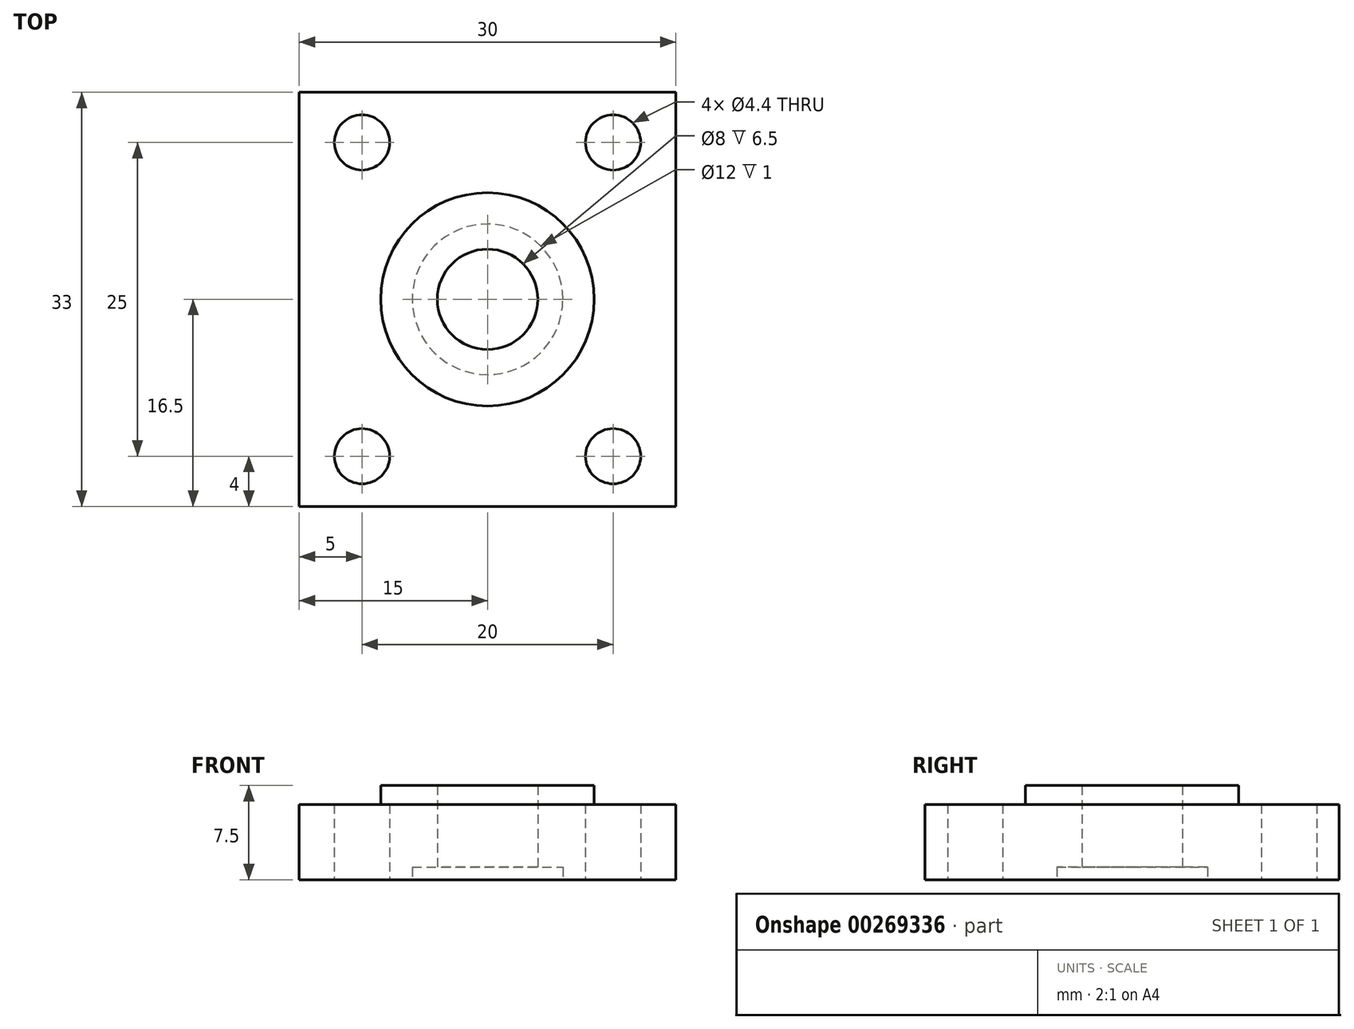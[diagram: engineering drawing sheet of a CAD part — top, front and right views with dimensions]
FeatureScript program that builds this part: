
annotation { "Feature Type Name" : "Feature", "Feature Type Description" : "" }
export const myFeature = defineFeature(function(context is Context, id is Id, definition is map)
    precondition{}
    {
        {
            var Q0;
            Q0=qCreatedBy(makeId("Top.planeOp"),FACE);
            var sketch = newSketch(context, id + "F0", { "sketchPlane" : qUnion([Q0])});
            skLineSegment(sketch, "E0.bottom", {"start": v(-15, -16.5) * mm, "end": v(15, -16.5) * mm});
            skLineSegment(sketch, "E0.top", {"start": v(-15, 16.5) * mm, "end": v(15, 16.5) * mm});
            skLineSegment(sketch, "E0.left", {"start": v(-15, -16.5) * mm, "end": v(-15, 16.5) * mm});
            skLineSegment(sketch, "E0.right", {"start": v(15, -16.5) * mm, "end": v(15, 16.5) * mm});
            skPoint(sketch, "E0.middle", {"position": v(0, 0) * mm});
            skCircle(sketch, "E1", {"center": v(0, 0) * mm, "radius": 4 * mm});
            skSolve(sketch);
        }
        {
            var Q0;
            Q0=qSketchRegion(id+"F0",true);
            extrude(context, id + "F1", {"entities" : qUnion([Q0]), "depth" : 6 * mm});
        }
        {
            var Q0;
            Q0=makeQuery(id+"F1.opExtrude","CAP_FACE",FACE,{"disambiguationData":[OSD([sQuery(id+"F0.wireOp",EDGE,"E0.bottom"),sQuery(id+"F0.wireOp",EDGE,"E0.top"),sQuery(id+"F0.wireOp",EDGE,"E0.left"),sQuery(id+"F0.wireOp",EDGE,"E0.right"),sQuery(id+"F0.wireOp",EDGE,"E1")])],"isStart":false});
            var sketch = newSketch(context, id + "F2", { "sketchPlane" : qUnion([Q0])});
            skCircle(sketch, "E2", {"center": v(0, 0) * mm, "radius": 4 * mm});
            skCircle(sketch, "E3", {"center": v(0, 0) * mm, "radius": 8.5 * mm});
            skSolve(sketch);
        }
        {
            var Q0;
            Q0=qSketchRegion(id+"F2",true);
            extrude(context, id + "F3", {"entities" : qUnion([Q0]), "operationType" : NewBodyOperationType.ADD, "depth" : 1.5 * mm});
        }
        {
            var Q0;
            Q0=makeQuery(id+"F1.opExtrude","CAP_FACE",FACE,{"disambiguationData":[OSD([sQuery(id+"F0.wireOp",EDGE,"E0.bottom"),sQuery(id+"F0.wireOp",EDGE,"E0.top"),sQuery(id+"F0.wireOp",EDGE,"E0.left"),sQuery(id+"F0.wireOp",EDGE,"E0.right"),sQuery(id+"F0.wireOp",EDGE,"E1")])],"isStart":true});
            var sketch = newSketch(context, id + "F4", { "sketchPlane" : qUnion([Q0])});
            skCircle(sketch, "E4", {"center": v(0, 0) * mm, "radius": 6 * mm});
            skCircle(sketch, "E5", {"center": v(0, 0) * mm, "radius": 4 * mm});
            skSolve(sketch);
        }
        {
            var Q0;
            Q0=qSketchRegion(id+"F4",true);
            extrude(context, id + "F5", {"entities" : qUnion([Q0]), "operationType" : NewBodyOperationType.REMOVE, "oppositeDirection" : true, "depth" : 1 * mm});
        }
        {
            var Q0;
            Q0=makeQuery(id+"F1.opExtrude","CAP_FACE",FACE,{"disambiguationData":[OSD([sQuery(id+"F0.wireOp",EDGE,"E0.bottom"),sQuery(id+"F0.wireOp",EDGE,"E0.top"),sQuery(id+"F0.wireOp",EDGE,"E0.left"),sQuery(id+"F0.wireOp",EDGE,"E0.right"),sQuery(id+"F0.wireOp",EDGE,"E1")])],"isStart":false});
            var sketch = newSketch(context, id + "F6", { "sketchPlane" : qUnion([Q0])});
            skLineSegment(sketch, "E6", {"start": v(-10, 12.5) * mm, "end": v(10, 12.5) * mm, "construction": true});
            skLineSegment(sketch, "E7", {"start": v(10, 12.5) * mm, "end": v(10, -12.5) * mm, "construction": true});
            skLineSegment(sketch, "E8", {"start": v(10, -12.5) * mm, "end": v(-10, -12.5) * mm, "construction": true});
            skLineSegment(sketch, "E9", {"start": v(-10, -12.5) * mm, "end": v(-10, 12.5) * mm, "construction": true});
            skLineSegment(sketch, "E10", {"start": v(-10, 0) * mm, "end": v(10, 0) * mm, "construction": true});
            skLineSegment(sketch, "E11", {"start": v(0, 12.5) * mm, "end": v(0, -12.5) * mm, "construction": true});
            skSolve(sketch);
        }
        {
            var Q0;
            Q0=sQuery(id+"F6.wireOp",VERTEX,"E9.end");
            var Q1;
            Q1=sQuery(id+"F6.wireOp",VERTEX,"E7.start");
            var Q2;
            Q2=sQuery(id+"F6.wireOp",VERTEX,"E8.start");
            var Q3;
            Q3=sQuery(id+"F6.wireOp",VERTEX,"E9.start");
            var Q4;
            Q4=makeQuery(id+"F1.opExtrude","SWEPT_BODY",BODY,{"disambiguationData":[OSD([sQuery(id+"F0.wireOp",EDGE,"E0.bottom"),sQuery(id+"F0.wireOp",EDGE,"E0.top"),sQuery(id+"F0.wireOp",EDGE,"E0.left"),sQuery(id+"F0.wireOp",EDGE,"E0.right"),sQuery(id+"F0.wireOp",EDGE,"E1")])]});
            hole(context, id + "F7", {"style" : HoleStyle.SIMPLE, "endStyle" : HoleEndStyle.THROUGH, "standardTappedOrClearance" : lookupTablePath({ "standard" : "ISO", "fit" : "Normal", "size" : "M4", "type" : "Clearance" }), "standardBlindInLast" : lookupTablePath({ "fit" : "Standard", "standard" : "ISO", "size" : "M4", "type" : "Clearance" }), "holeDiameter" : 4.4 * mm, "locations" : qUnion([Q0, Q1, Q2, Q3]), "scope" : qUnion([Q4]), "isTappedThrough" : true});
        }
    });
